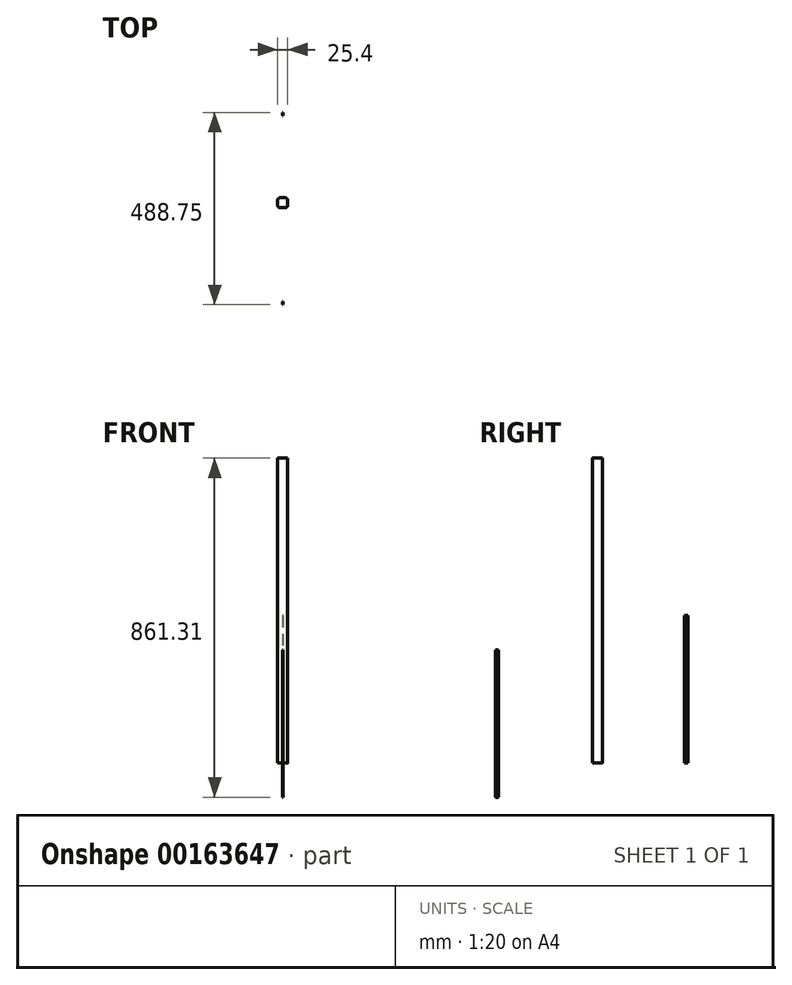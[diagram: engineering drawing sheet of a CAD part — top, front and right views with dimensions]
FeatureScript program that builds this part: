
annotation { "Feature Type Name" : "Feature", "Feature Type Description" : "" }
export const myFeature = defineFeature(function(context is Context, id is Id, definition is map)
    precondition{}
    {
        {
            var Q0;
            Q0=qCreatedBy(makeId("Top.planeOp"),FACE);
            var sketch = newSketch(context, id + "F0", { "sketchPlane" : qUnion([Q0])});
            skLineSegment(sketch, "E0.bottom", {"start": v(6.35, 12.7) * mm, "end": v(-6.35, 12.7) * mm});
            skLineSegment(sketch, "E0.top", {"start": v(6.35, -12.7) * mm, "end": v(-6.35, -12.7) * mm});
            skLineSegment(sketch, "E0.left", {"start": v(12.7, 6.35) * mm, "end": v(12.7, -6.35) * mm});
            skLineSegment(sketch, "E0.right", {"start": v(-12.7, 6.35) * mm, "end": v(-12.7, -6.35) * mm});
            skPoint(sketch, "E0.middle", {"position": v(0, 0) * mm});
            skPoint(sketch, "E1.visualSharp", {"position": v(-12.7, 12.7) * mm});
            skArc(sketch, "E1.filletArc", {"start": v(-6.35, 12.7) * mm, "mid": v(-10.84, 10.84) * mm, "end": v(-12.7, 6.35) * mm});
            skPoint(sketch, "E2.visualSharp", {"position": v(-12.7, -12.7) * mm});
            skArc(sketch, "E2.filletArc", {"start": v(-12.7, -6.35) * mm, "mid": v(-10.84, -10.84) * mm, "end": v(-6.35, -12.7) * mm});
            skPoint(sketch, "E3.visualSharp", {"position": v(12.7, -12.7) * mm});
            skArc(sketch, "E3.filletArc", {"start": v(6.35, -12.7) * mm, "mid": v(10.84, -10.84) * mm, "end": v(12.7, -6.35) * mm});
            skPoint(sketch, "E4.visualSharp", {"position": v(12.7, 12.7) * mm});
            skArc(sketch, "E4.filletArc", {"start": v(12.7, 6.35) * mm, "mid": v(10.84, 10.84) * mm, "end": v(6.35, 12.7) * mm});
            skSolve(sketch);
        }
        {
            var Q0;
            Q0=qSketchRegion(id+"F0",true);
            extrude(context, id + "F1", {"entities" : qUnion([Q0]), "depth" : 774.7 * mm});
        }
        {
            var Q0;
            Q0=qCreatedBy(makeId("Right.planeOp"),FACE);
            var sketch = newSketch(context, id + "F2", { "sketchPlane" : qUnion([Q0])});
            skLineSegment(sketch, "E5.bottom", {"start": v(-259, 288.04) * mm, "end": v(-250.53, 288.04) * mm});
            skLineSegment(sketch, "E5.top", {"start": v(-259, -86.61) * mm, "end": v(-250.53, -86.61) * mm});
            skLineSegment(sketch, "E5.left", {"start": v(-259, 288.04) * mm, "end": v(-259, -86.61) * mm});
            skLineSegment(sketch, "E5.right", {"start": v(-250.53, 288.04) * mm, "end": v(-250.53, -86.61) * mm});
            skSolve(sketch);
        }
        {
            var Q0;
            Q0=makeQuery(id+"F2.imprint","IMPRINT",FACE,{"disambiguationData":[TD([[makeQuery(id+"F2.imprint","IMPRINT",EDGE,{"derivedFrom":sQuery(id+"F2.wireOp",EDGE,"E5.bottom")}),-1.0]])]});
            extrude(context, id + "F3", {"entities" : qUnion([Q0]), "depth" : 1.27 * mm});
        }
        {
            var Q0;
            Q0=qCreatedBy(makeId("Right.planeOp"),FACE);
            var sketch = newSketch(context, id + "F4", { "sketchPlane" : qUnion([Q0])});
            skLineSegment(sketch, "E6.bottom", {"start": v(221.29, 374.65) * mm, "end": v(229.75, 374.65) * mm});
            skLineSegment(sketch, "E6.top", {"start": v(221.29, 0) * mm, "end": v(229.75, 0) * mm});
            skLineSegment(sketch, "E6.left", {"start": v(221.29, 374.65) * mm, "end": v(221.29, 0) * mm});
            skLineSegment(sketch, "E6.right", {"start": v(229.75, 374.65) * mm, "end": v(229.75, 0) * mm});
            skSolve(sketch);
        }
        {
            var Q0;
            Q0=makeQuery(id+"F4.imprint","IMPRINT",FACE,{"disambiguationData":[TD([[makeQuery(id+"F4.imprint","IMPRINT",EDGE,{"derivedFrom":sQuery(id+"F4.wireOp",EDGE,"E6.bottom")}),-1.0]])]});
            var Q1;
            Q1=sQuery(id+"F4.wireOp",EDGE,"E6.right");
            var Q2;
            Q2=sQuery(id+"F4.wireOp",EDGE,"E6.left");
            var Q3;
            Q3=sQuery(id+"F4.wireOp",EDGE,"E6.top");
            var Q4;
            Q4=sQuery(id+"F4.wireOp",EDGE,"E6.bottom");
            extrude(context, id + "F5", {"entities" : qUnion([Q0]), "surfaceEntities" : qUnion([Q1, Q2, Q3, Q4]), "depth" : 1.27 * mm});
        }
    });
